# Revit family: rs_pro_led_s2_035853
name_source: partatom
category: Leuchten
revit_build: Autodesk Revit 2016 (Build: 20190508_0715(x64)
units: mm (PartAtom-declared; Revit-internal decimal feet)

## family parameters
Basisbauteil = Fläche
Beim Laden mit Abzugskörper schneiden = Nein
Bemaßung runder Anschluss = Durchmesser verwenden
Gemeinsam genutzt = Nein
Lichtquelle = Nein
Raumberechnungspunkt = Nein
Teiletyp = Normal

## types (1)
- RS PRO LED S2 (1 x , 1950 lm, 3000 K)
    Beschreibung = Dimensions (Ø x H): 362 x 85 mm; Mains power supply: 230 – 240 V / 50 – 60 Hz; Sensor Technology: High frequency; Transmitter power: < 1 mW; HF-system: 5,8 GHz; Output: 26 W; Interconnection: Yes; Type of interconnection: Master/master, Master/slave; Luminous flux: 1950 lm; Colour temperature: 3000 K; Colour variation LED: SDCM3; Colour Rendering Index CRI: 80-89; With lamp: Yes, STEINEL LED system; Lamp: LED cannot be replaced; LED life expectancy (max. °C): 70000 h; Drop in luminous flux in accordance with LM80: L80B10; Base: GX24d-3; LED cooling system: Active Thermo Control; With motion detector: Yes; Detection: also through glass, wood and stud walls; Detection angle: 360 °; Angle of aperture: 160 °; Capability of masking out individual segments: Yes; Electronic scalability: Yes; Mechanical scalability: No; Reach, radial: Ø 8 m (50 m²); Reach, tangential: Ø 8 m (50 m²); Main light adjustable: 10 - 100 %; Continuous light: selectable, 4h; Photo-cell controller: Yes; Twilight setting: 2 – 2000 lx; Time setting: 5 sec – 15 min; Basic light level function: Yes; Basic light level function time: 10/30 min, all night; Functions: Neighbouring-group function, Presence function, Group parameterisation, Manual ON / ON-OFF; Soft light start: Yes; Impact resistance: IK03; IP-rating: IP20; Protection class: II; Ambient temperature: -10 – 50 °C; Housing material: Aluminium; Cover material: Glass opal; Manufacturer's Warranty: 5 years; Settings via: DIP switches, Potentiometers, Remote control, Smart Remote; With remote control: No; Version: Glass warm white; PU1, EAN: 4007841035853
    CIE Flux Codes = 44 74 92 96 99
    Color Rendering = 80-89
    Color Temperature = 3000 K
    Frequency = 60 Hz, 50 Hz
    Height = 0 mm  [stored 0 ft]
    Hersteller = Steinel
    Lamp Light Flux = 1950 lm
    Lamp count = 1
    Lampe = 1 x
    Length = 362 mm
    Luminous efficacy = 75 lm/W
    ModVariant = Nein
    Modell = 035853
    Mounting Type = Surface mounted
    Number of Poles = 1
    OnlyDefault = Ja
    Power Factor = 1
    Product Name = RS PRO LED S2
    Product group = Sensor-switched indoor light
    ProductGroupID = 30
    Protection Class = Protection class II
    Protection Degree = IP 20
    RlxData = <blob elided: 83801 chars, md5=539297ac>
    Scheinlast = 26 VA
    Socket = socket
    Standby Power = 0 W
    System Light Flux = 1938 lm
    System Power = 26 W
    Typenbild = produkt1_035853.jpg
    Typenkommentare = Product without accessories
    URL = http://relux.com
    VarID = ---
    Voltage = 0 V
    Vorgabe-Ansicht = 1800 mm
    Weight = 0.00 kg
    Width = 0 mm  [stored 0 ft]

note: [stored X ft] marks values corroborated as IEEE doubles in the binary element streams (Revit-internal decimal feet)

## geometry (parser evidence)
native form markers: Blend x4, Sweep x12
no freeform markers — native parametric forms only
